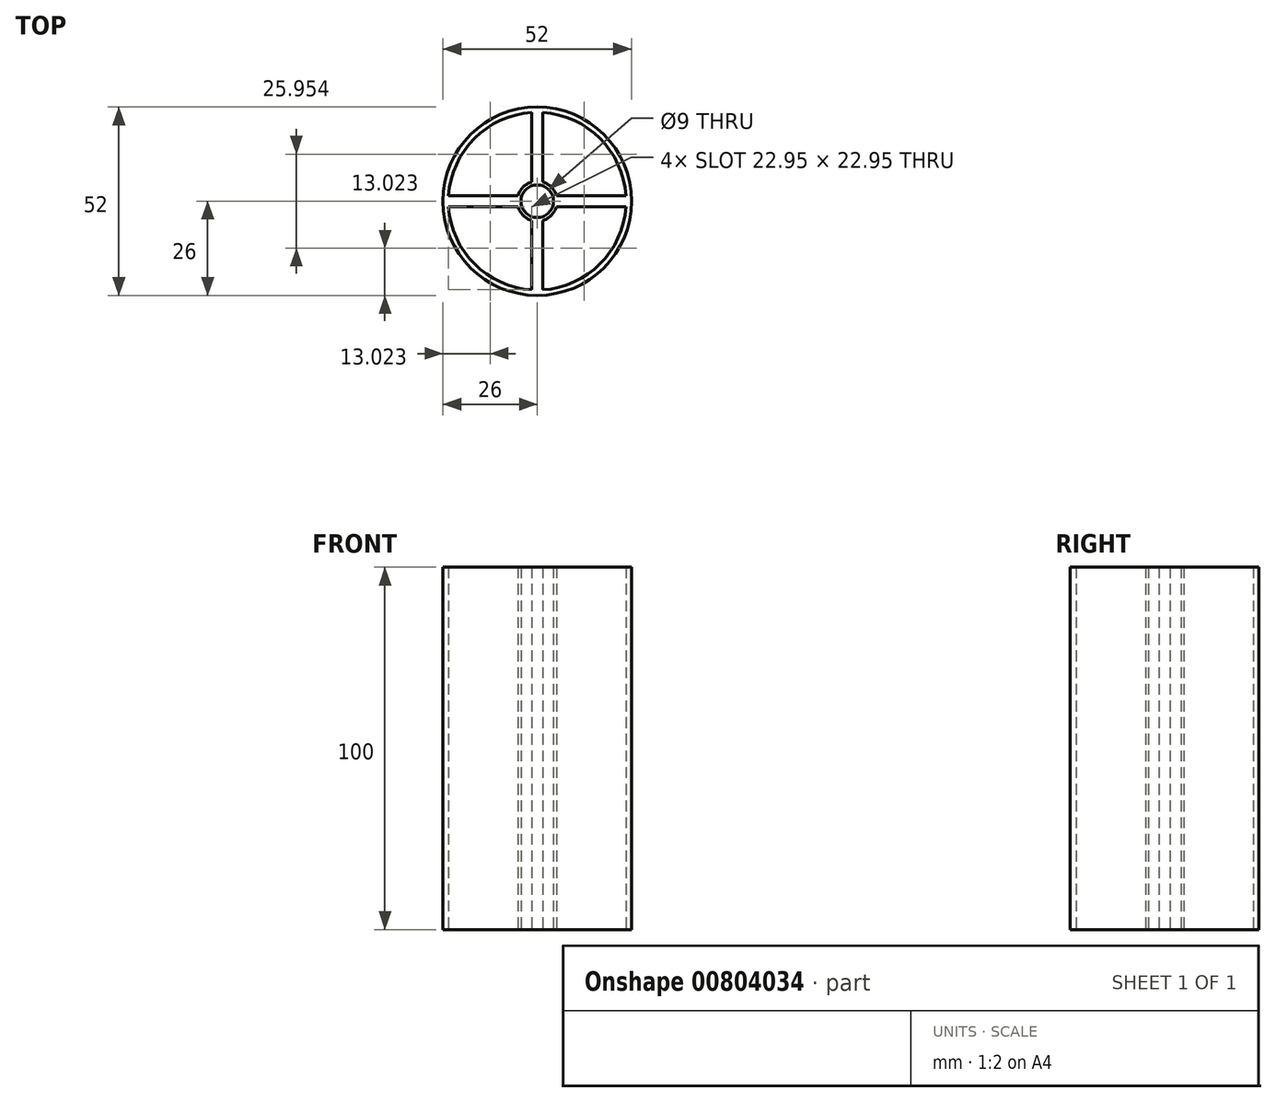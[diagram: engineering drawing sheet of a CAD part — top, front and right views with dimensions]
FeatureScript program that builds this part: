
annotation { "Feature Type Name" : "Feature", "Feature Type Description" : "" }
export const myFeature = defineFeature(function(context is Context, id is Id, definition is map)
    precondition{}
    {
        {
            var Q0;
            Q0=qCreatedBy(makeId("Top.planeOp"),FACE);
            var sketch = newSketch(context, id + "F0", { "sketchPlane" : qUnion([Q0])});
            skCircle(sketch, "E0", {"center": v(0, 0) * mm, "radius": 26 * mm});
            skCircle(sketch, "E1", {"center": v(0, 0) * mm, "radius": 24.5 * mm});
            skCircle(sketch, "E2", {"center": v(0, 0) * mm, "radius": 5.5 * mm});
            skCircle(sketch, "E3", {"center": v(0, 0) * mm, "radius": 4.5 * mm});
            skLineSegment(sketch, "E4", {"start": v(0, 5.5) * mm, "end": v(0, 24.5) * mm});
            skLineSegment(sketch, "E5", {"start": v(1.5, 24.45) * mm, "end": v(1.5, 5.3) * mm});
            skLineSegment(sketch, "E6", {"start": v(-1.5, 5.3) * mm, "end": v(-1.5, 24.45) * mm});
            skLineSegment(sketch, "E7", {"start": v(5.5, 0) * mm, "end": v(24.5, 0) * mm});
            skLineSegment(sketch, "E8", {"start": v(0, -5.5) * mm, "end": v(0, -24.5) * mm});
            skLineSegment(sketch, "E9", {"start": v(-5.5, 0) * mm, "end": v(-24.5, 0) * mm});
            skLineSegment(sketch, "E10", {"start": v(5.3, 1.5) * mm, "end": v(24.45, 1.5) * mm});
            skLineSegment(sketch, "E11", {"start": v(24.45, -1.5) * mm, "end": v(5.3, -1.5) * mm});
            skLineSegment(sketch, "E12", {"start": v(-1.5, -5.3) * mm, "end": v(-1.5, -24.45) * mm});
            skLineSegment(sketch, "E13", {"start": v(-5.3, -1.5) * mm, "end": v(-24.45, -1.5) * mm});
            skLineSegment(sketch, "E14", {"start": v(-24.45, 1.5) * mm, "end": v(-5.3, 1.5) * mm});
            skLineSegment(sketch, "E15", {"start": v(1.5, -24.45) * mm, "end": v(1.5, -5.3) * mm});
            skSolve(sketch);
        }
        {
            var Q0;
            Q0=makeQuery(id+"F0.imprint","IMPRINT",FACE,{"disambiguationData":[TD([[makeQuery(id+"F0.imprint","IMPRINT",EDGE,{"derivedFrom":sQuery(id+"F0.wireOp",EDGE,"E0")}),1.0]])]});
            var Q1;
            {var subQ0=sQuery(id+"F0.wireOp",EDGE,"E4");Q1=makeQuery(id+"F0.imprint","IMPRINT",FACE,{"disambiguationData":[TD([[makeQuery(id+"F0.imprint","IMPRINT",EDGE,{"derivedFrom":subQ0}),1.0]])]});}
            var Q2;
            {var subQ0=sQuery(id+"F0.wireOp",EDGE,"E4");Q2=makeQuery(id+"F0.imprint","IMPRINT",FACE,{"disambiguationData":[TD([[makeQuery(id+"F0.imprint","IMPRINT",EDGE,{"derivedFrom":subQ0}),-1.0]])]});}
            var Q3;
            Q3=makeQuery(id+"F0.imprint","IMPRINT",FACE,{"disambiguationData":[TD([[makeQuery(id+"F0.imprint","IMPRINT",EDGE,{"derivedFrom":sQuery(id+"F0.wireOp",EDGE,"E3")}),-1.0]])]});
            var Q4;
            {var subQ0=sQuery(id+"F0.wireOp",EDGE,"E7");Q4=makeQuery(id+"F0.imprint","IMPRINT",FACE,{"disambiguationData":[TD([[makeQuery(id+"F0.imprint","IMPRINT",EDGE,{"derivedFrom":subQ0}),1.0]])]});}
            var Q5;
            {var subQ0=sQuery(id+"F0.wireOp",EDGE,"E7");Q5=makeQuery(id+"F0.imprint","IMPRINT",FACE,{"disambiguationData":[TD([[makeQuery(id+"F0.imprint","IMPRINT",EDGE,{"derivedFrom":subQ0}),-1.0]])]});}
            var Q6;
            {var subQ0=sQuery(id+"F0.wireOp",EDGE,"E8");Q6=makeQuery(id+"F0.imprint","IMPRINT",FACE,{"disambiguationData":[TD([[makeQuery(id+"F0.imprint","IMPRINT",EDGE,{"derivedFrom":subQ0}),-1.0]])]});}
            var Q7;
            {var subQ0=sQuery(id+"F0.wireOp",EDGE,"E9");Q7=makeQuery(id+"F0.imprint","IMPRINT",FACE,{"disambiguationData":[TD([[makeQuery(id+"F0.imprint","IMPRINT",EDGE,{"derivedFrom":subQ0}),-1.0]])]});}
            var Q8;
            {var subQ0=sQuery(id+"F0.wireOp",EDGE,"E9");Q8=makeQuery(id+"F0.imprint","IMPRINT",FACE,{"disambiguationData":[TD([[makeQuery(id+"F0.imprint","IMPRINT",EDGE,{"derivedFrom":subQ0}),1.0]])]});}
            var Q9;
            {var subQ0=sQuery(id+"F0.wireOp",EDGE,"E8");Q9=makeQuery(id+"F0.imprint","IMPRINT",FACE,{"disambiguationData":[TD([[makeQuery(id+"F0.imprint","IMPRINT",EDGE,{"derivedFrom":subQ0}),1.0]])]});}
            extrude(context, id + "F1", {"entities" : qUnion([Q0, Q1, Q2, Q3, Q4, Q5, Q6, Q7, Q8, Q9]), "depth" : 100 * mm, "offsetDistance" : 25 * mm});
        }
    });
